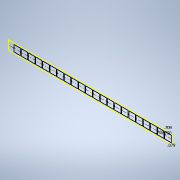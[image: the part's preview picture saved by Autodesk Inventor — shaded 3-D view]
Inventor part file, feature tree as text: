
AUTODESK INVENTOR PART (.ipt)
format: ipt  version: 2022 (Build 260153000, 153)  size: 122,368 bytes
history: native  units: in
note: dims shown in document units (in); Inventor stores cm internally (conversion verified against a paired STEP export)
features: reference x2, other x2, sketch x1
ambient origin geometry x8: Origin, YZ Plane, XZ Plane, XY Plane, X Axis, Y Axis, Z Axis, Center Point
feature tree (5):
  sketch  "Sketch1"  dims[d0=0.7087in d1=0.7087in d2=0.0787in d3=8.6614in d5=0.79in d6=0.3937in d8=1.0in]
  reference  "Reference1"
  reference  "Reference2"
  other  "Assembly1"
  other  "Stock:1"
